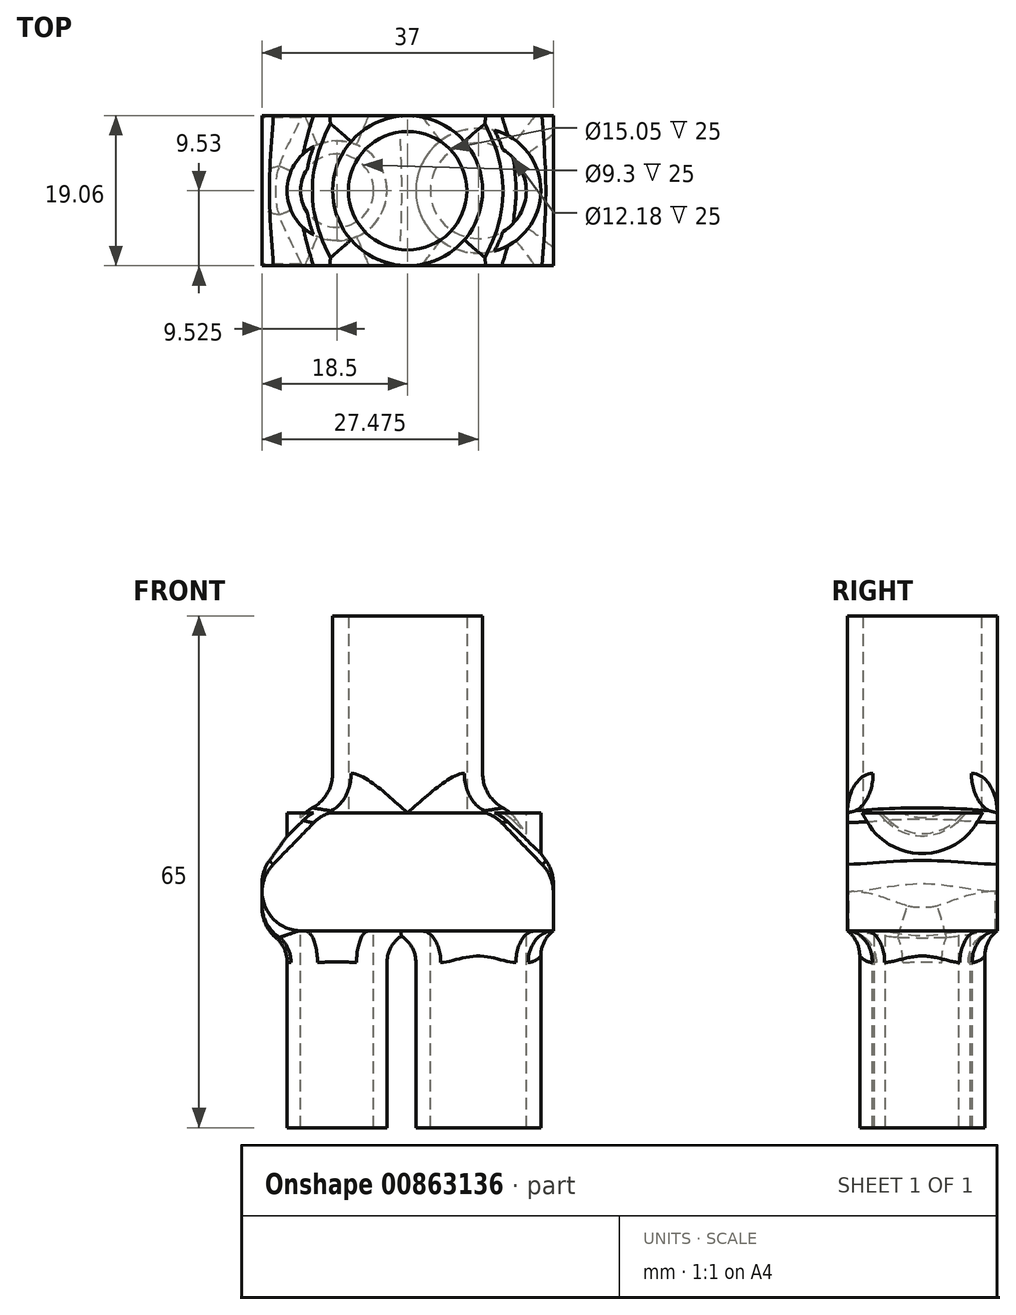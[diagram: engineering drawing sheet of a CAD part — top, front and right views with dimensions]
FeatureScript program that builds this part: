
annotation { "Feature Type Name" : "Feature", "Feature Type Description" : "" }
export const myFeature = defineFeature(function(context is Context, id is Id, definition is map)
    precondition{}
    {
        {
            var Q0;
            Q0=qCreatedBy(makeId("Top.planeOp"),FACE);
            var sketch = newSketch(context, id + "F0", { "sketchPlane" : qUnion([Q0])});
            skCircle(sketch, "E0", {"center": v(0, 0) * mm, "radius": 9.53 * mm});
            skCircle(sketch, "E1", {"center": v(0, 0) * mm, "radius": 7.53 * mm});
            skLineSegment(sketch, "E2.bottom", {"start": v(18.5, 9.53) * mm, "end": v(-18.5, 9.53) * mm});
            skLineSegment(sketch, "E2.top", {"start": v(18.5, -9.53) * mm, "end": v(-18.5, -9.53) * mm});
            skLineSegment(sketch, "E2.left", {"start": v(18.5, 9.53) * mm, "end": v(18.5, -9.53) * mm});
            skLineSegment(sketch, "E2.right", {"start": v(-18.5, 9.53) * mm, "end": v(-18.5, -9.53) * mm});
            skPoint(sketch, "E3", {"position": v(-8.98, 0) * mm});
            skPoint(sketch, "E4", {"position": v(8.97, 0) * mm});
            skCircle(sketch, "E5", {"center": v(-8.98, 0) * mm, "radius": 6.35 * mm});
            skCircle(sketch, "E6", {"center": v(8.97, 0) * mm, "radius": 7.94 * mm});
            skCircle(sketch, "E7", {"center": v(-8.98, 0) * mm, "radius": 4.65 * mm});
            skCircle(sketch, "E8", {"center": v(8.97, 0) * mm, "radius": 6.09 * mm});
            skSolve(sketch);
        }
        {
            var Q0;
            Q0=makeQuery(id+"F0.imprint","IMPRINT",FACE,{"disambiguationData":[TD([[makeQuery(id+"F0.imprint","IMPRINT",EDGE,{"derivedFrom":sQuery(id+"F0.wireOp",EDGE,"E0")}),1.0]])]});
            var Q1;
            {var subQ0=sQuery(id+"F0.wireOp",EDGE,"E7");var subQ1=sQuery(id+"F0.wireOp",EDGE,"E0");var subQ2=makeQuery(id+"F0.imprint","INTERSECT",VERTEX,{"disambiguationData":[OD(0.0)],"derivedFrom":[subQ1,subQ0]});Q1=makeQuery(id+"F0.imprint","IMPRINT",FACE,{"disambiguationData":[TD([[makeQuery(id+"F0.imprint","IMPRINT",EDGE,{"disambiguationData":[TD([[subQ2,-1.0]])],"derivedFrom":subQ1}),1.0]])]});}
            var Q2;
            {var subQ0=sQuery(id+"F0.wireOp",EDGE,"E7");var subQ1=sQuery(id+"F0.wireOp",EDGE,"E0");var subQ2=makeQuery(id+"F0.imprint","INTERSECT",VERTEX,{"disambiguationData":[OD(1.0)],"derivedFrom":[subQ1,subQ0]});Q2=makeQuery(id+"F0.imprint","IMPRINT",FACE,{"disambiguationData":[TD([[makeQuery(id+"F0.imprint","IMPRINT",EDGE,{"disambiguationData":[TD([[subQ2,-1.0]])],"derivedFrom":subQ1}),1.0]])]});}
            var Q3;
            {var subQ0=sQuery(id+"F0.wireOp",EDGE,"E6");var subQ1=sQuery(id+"F0.wireOp",EDGE,"E0");var subQ2=makeQuery(id+"F0.imprint","INTERSECT",VERTEX,{"disambiguationData":[OD(1.0)],"derivedFrom":[subQ1,subQ0]});Q3=makeQuery(id+"F0.imprint","IMPRINT",FACE,{"disambiguationData":[TD([[makeQuery(id+"F0.imprint","IMPRINT",EDGE,{"disambiguationData":[TD([[subQ2,-1.0]])],"derivedFrom":subQ1}),1.0]])]});}
            var Q4;
            {var subQ0=sQuery(id+"F0.wireOp",EDGE,"E8");var subQ1=sQuery(id+"F0.wireOp",EDGE,"E0");var subQ2=makeQuery(id+"F0.imprint","INTERSECT",VERTEX,{"disambiguationData":[OD(0.0)],"derivedFrom":[subQ1,subQ0]});Q4=makeQuery(id+"F0.imprint","IMPRINT",FACE,{"disambiguationData":[TD([[makeQuery(id+"F0.imprint","IMPRINT",EDGE,{"disambiguationData":[TD([[subQ2,1.0]])],"derivedFrom":subQ1}),1.0]])]});}
            var Q5;
            {var subQ0=sQuery(id+"F0.wireOp",EDGE,"E6");var subQ1=sQuery(id+"F0.wireOp",EDGE,"E0");var subQ2=makeQuery(id+"F0.imprint","INTERSECT",VERTEX,{"disambiguationData":[OD(0.0)],"derivedFrom":[subQ1,subQ0]});Q5=makeQuery(id+"F0.imprint","IMPRINT",FACE,{"disambiguationData":[TD([[makeQuery(id+"F0.imprint","IMPRINT",EDGE,{"disambiguationData":[TD([[subQ2,1.0]])],"derivedFrom":subQ1}),1.0]])]});}
            var Q6;
            {var subQ0=sQuery(id+"F0.wireOp",EDGE,"E5");var subQ1=sQuery(id+"F0.wireOp",EDGE,"E0");var subQ2=makeQuery(id+"F0.imprint","INTERSECT",VERTEX,{"disambiguationData":[OD(0.0)],"derivedFrom":[subQ1,subQ0]});Q6=makeQuery(id+"F0.imprint","IMPRINT",FACE,{"disambiguationData":[TD([[makeQuery(id+"F0.imprint","IMPRINT",EDGE,{"disambiguationData":[TD([[subQ2,-1.0]])],"derivedFrom":subQ1}),1.0]])]});}
            extrude(context, id + "F1", {"entities" : qUnion([Q0, Q1, Q2, Q3, Q4, Q5, Q6]), "depth" : 25 * mm, "offsetDistance" : 25 * mm});
        }
        {
            var Q0;
            {var subQ0=sQuery(id+"F0.wireOp",EDGE,"E6");var subQ1=sQuery(id+"F0.wireOp",EDGE,"E1");var subQ2=makeQuery(id+"F0.imprint","INTERSECT",VERTEX,{"disambiguationData":[OD(0.0)],"derivedFrom":[subQ1,subQ0]});Q0=makeQuery(id+"F0.imprint","IMPRINT",FACE,{"disambiguationData":[TD([[makeQuery(id+"F0.imprint","IMPRINT",EDGE,{"disambiguationData":[TD([[subQ2,1.0]])],"derivedFrom":subQ1}),1.0]])]});}
            var Q1;
            {var subQ0=sQuery(id+"F0.wireOp",EDGE,"E5");var subQ1=sQuery(id+"F0.wireOp",EDGE,"E1");var subQ2=makeQuery(id+"F0.imprint","INTERSECT",VERTEX,{"disambiguationData":[OD(0.0)],"derivedFrom":[subQ1,subQ0]});Q1=makeQuery(id+"F0.imprint","IMPRINT",FACE,{"disambiguationData":[TD([[makeQuery(id+"F0.imprint","IMPRINT",EDGE,{"disambiguationData":[TD([[subQ2,-1.0]])],"derivedFrom":subQ1}),1.0]])]});}
            var Q2;
            {var subQ0=sQuery(id+"F0.wireOp",EDGE,"E2.right");Q2=makeQuery(id+"F0.imprint","IMPRINT",FACE,{"disambiguationData":[TD([[makeQuery(id+"F0.imprint","IMPRINT",EDGE,{"derivedFrom":subQ0}),1.0]])]});}
            var Q3;
            {var subQ0=sQuery(id+"F0.wireOp",EDGE,"E2.left");Q3=makeQuery(id+"F0.imprint","IMPRINT",FACE,{"disambiguationData":[TD([[makeQuery(id+"F0.imprint","IMPRINT",EDGE,{"derivedFrom":subQ0}),-1.0]])]});}
            var Q4;
            {var subQ0=sQuery(id+"F0.wireOp",EDGE,"E6");var subQ1=sQuery(id+"F0.wireOp",EDGE,"E0");var subQ2=makeQuery(id+"F0.imprint","INTERSECT",VERTEX,{"disambiguationData":[OD(0.0)],"derivedFrom":[subQ1,subQ0]});Q4=makeQuery(id+"F0.imprint","IMPRINT",FACE,{"disambiguationData":[TD([[makeQuery(id+"F0.imprint","IMPRINT",EDGE,{"disambiguationData":[TD([[subQ2,1.0]])],"derivedFrom":subQ1}),1.0]])]});}
            var Q5;
            {var subQ0=sQuery(id+"F0.wireOp",EDGE,"E5");var subQ1=sQuery(id+"F0.wireOp",EDGE,"E0");var subQ2=makeQuery(id+"F0.imprint","INTERSECT",VERTEX,{"disambiguationData":[OD(0.0)],"derivedFrom":[subQ1,subQ0]});Q5=makeQuery(id+"F0.imprint","IMPRINT",FACE,{"disambiguationData":[TD([[makeQuery(id+"F0.imprint","IMPRINT",EDGE,{"disambiguationData":[TD([[subQ2,-1.0]])],"derivedFrom":subQ1}),1.0]])]});}
            var Q6;
            {var subQ0=sQuery(id+"F0.wireOp",EDGE,"E7");var subQ1=sQuery(id+"F0.wireOp",EDGE,"E0");var subQ2=makeQuery(id+"F0.imprint","INTERSECT",VERTEX,{"disambiguationData":[OD(0.0)],"derivedFrom":[subQ1,subQ0]});Q6=makeQuery(id+"F0.imprint","IMPRINT",FACE,{"disambiguationData":[TD([[makeQuery(id+"F0.imprint","IMPRINT",EDGE,{"disambiguationData":[TD([[subQ2,-1.0]])],"derivedFrom":subQ1}),1.0]])]});}
            var Q7;
            {var subQ0=sQuery(id+"F0.wireOp",EDGE,"E7");var subQ1=sQuery(id+"F0.wireOp",EDGE,"E0");var subQ2=makeQuery(id+"F0.imprint","INTERSECT",VERTEX,{"disambiguationData":[OD(1.0)],"derivedFrom":[subQ1,subQ0]});Q7=makeQuery(id+"F0.imprint","IMPRINT",FACE,{"disambiguationData":[TD([[makeQuery(id+"F0.imprint","IMPRINT",EDGE,{"disambiguationData":[TD([[subQ2,-1.0]])],"derivedFrom":subQ1}),1.0]])]});}
            var Q8;
            {var subQ0=sQuery(id+"F0.wireOp",EDGE,"E6");var subQ1=sQuery(id+"F0.wireOp",EDGE,"E0");var subQ2=makeQuery(id+"F0.imprint","INTERSECT",VERTEX,{"disambiguationData":[OD(1.0)],"derivedFrom":[subQ1,subQ0]});Q8=makeQuery(id+"F0.imprint","IMPRINT",FACE,{"disambiguationData":[TD([[makeQuery(id+"F0.imprint","IMPRINT",EDGE,{"disambiguationData":[TD([[subQ2,-1.0]])],"derivedFrom":subQ1}),1.0]])]});}
            var Q9;
            {var subQ0=sQuery(id+"F0.wireOp",EDGE,"E8");var subQ1=sQuery(id+"F0.wireOp",EDGE,"E0");var subQ2=makeQuery(id+"F0.imprint","INTERSECT",VERTEX,{"disambiguationData":[OD(0.0)],"derivedFrom":[subQ1,subQ0]});Q9=makeQuery(id+"F0.imprint","IMPRINT",FACE,{"disambiguationData":[TD([[makeQuery(id+"F0.imprint","IMPRINT",EDGE,{"disambiguationData":[TD([[subQ2,1.0]])],"derivedFrom":subQ1}),1.0]])]});}
            var Q10;
            {var subQ0=sQuery(id+"F0.wireOp",EDGE,"E7");var subQ1=sQuery(id+"F0.wireOp",EDGE,"E0");var subQ2=makeQuery(id+"F0.imprint","INTERSECT",VERTEX,{"disambiguationData":[OD(0.0)],"derivedFrom":[subQ1,subQ0]});Q10=makeQuery(id+"F0.imprint","IMPRINT",FACE,{"disambiguationData":[TD([[makeQuery(id+"F0.imprint","IMPRINT",EDGE,{"disambiguationData":[TD([[subQ2,-1.0]])],"derivedFrom":subQ1}),-1.0]])]});}
            var Q11;
            {var subQ0=sQuery(id+"F0.wireOp",EDGE,"E5");var subQ1=sQuery(id+"F0.wireOp",EDGE,"E0");var subQ2=makeQuery(id+"F0.imprint","INTERSECT",VERTEX,{"disambiguationData":[OD(0.0)],"derivedFrom":[subQ1,subQ0]});Q11=makeQuery(id+"F0.imprint","IMPRINT",FACE,{"disambiguationData":[TD([[makeQuery(id+"F0.imprint","IMPRINT",EDGE,{"disambiguationData":[TD([[subQ2,-1.0]])],"derivedFrom":subQ1}),-1.0]])]});}
            var Q12;
            {var subQ0=sQuery(id+"F0.wireOp",EDGE,"E8");var subQ1=sQuery(id+"F0.wireOp",EDGE,"E1");var subQ2=makeQuery(id+"F0.imprint","INTERSECT",VERTEX,{"disambiguationData":[OD(0.0)],"derivedFrom":[subQ1,subQ0]});Q12=makeQuery(id+"F0.imprint","IMPRINT",FACE,{"disambiguationData":[TD([[makeQuery(id+"F0.imprint","IMPRINT",EDGE,{"disambiguationData":[TD([[subQ2,1.0]])],"derivedFrom":subQ1}),1.0]])]});}
            var Q13;
            {var subQ0=sQuery(id+"F0.wireOp",EDGE,"E8");var subQ1=sQuery(id+"F0.wireOp",EDGE,"E0");var subQ2=makeQuery(id+"F0.imprint","INTERSECT",VERTEX,{"disambiguationData":[OD(0.0)],"derivedFrom":[subQ1,subQ0]});Q13=makeQuery(id+"F0.imprint","IMPRINT",FACE,{"disambiguationData":[TD([[makeQuery(id+"F0.imprint","IMPRINT",EDGE,{"disambiguationData":[TD([[subQ2,1.0]])],"derivedFrom":subQ1}),-1.0]])]});}
            var Q14;
            {var subQ0=sQuery(id+"F0.wireOp",EDGE,"E6");var subQ1=sQuery(id+"F0.wireOp",EDGE,"E0");var subQ2=makeQuery(id+"F0.imprint","INTERSECT",VERTEX,{"disambiguationData":[OD(0.0)],"derivedFrom":[subQ1,subQ0]});Q14=makeQuery(id+"F0.imprint","IMPRINT",FACE,{"disambiguationData":[TD([[makeQuery(id+"F0.imprint","IMPRINT",EDGE,{"disambiguationData":[TD([[subQ2,1.0]])],"derivedFrom":subQ1}),-1.0]])]});}
            var Q15;
            {var subQ0=sQuery(id+"F0.wireOp",EDGE,"E6");var subQ1=sQuery(id+"F0.wireOp",EDGE,"E1");var subQ2=makeQuery(id+"F0.imprint","INTERSECT",VERTEX,{"disambiguationData":[OD(0.0)],"derivedFrom":[subQ1,subQ0]});Q15=makeQuery(id+"F0.imprint","IMPRINT",FACE,{"disambiguationData":[TD([[makeQuery(id+"F0.imprint","IMPRINT",EDGE,{"disambiguationData":[TD([[subQ2,-1.0]])],"derivedFrom":subQ1}),1.0]])]});}
            var Q16;
            {var subQ5=sQuery(id+"F0.wireOp",EDGE,"E0");var subQ7=makeQuery(id+"F0.imprint","INTERSECT",VERTEX,{"derivedFrom":[subQ5,sQuery(id+"F0.wireOp",EDGE,"E2.top")]});Q16=makeQuery(id+"F0.imprint","IMPRINT",FACE,{"disambiguationData":[TD([[makeQuery(id+"F0.imprint","IMPRINT",EDGE,{"disambiguationData":[TD([[subQ7,1.0]])],"derivedFrom":subQ5}),1.0]])]});}
            var Q17;
            {var subQ1=sQuery(id+"F0.wireOp",EDGE,"E0");var subQ5=makeQuery(id+"F0.imprint","INTERSECT",VERTEX,{"derivedFrom":[subQ1,sQuery(id+"F0.wireOp",EDGE,"E2.bottom")]});Q17=makeQuery(id+"F0.imprint","IMPRINT",FACE,{"disambiguationData":[TD([[makeQuery(id+"F0.imprint","IMPRINT",EDGE,{"disambiguationData":[TD([[subQ5,1.0]])],"derivedFrom":subQ1}),1.0]])]});}
            var Q18;
            {var subQ0=sQuery(id+"F0.wireOp",EDGE,"E7");var subQ1=sQuery(id+"F0.wireOp",EDGE,"E1");var subQ2=makeQuery(id+"F0.imprint","INTERSECT",VERTEX,{"disambiguationData":[OD(0.0)],"derivedFrom":[subQ1,subQ0]});Q18=makeQuery(id+"F0.imprint","IMPRINT",FACE,{"disambiguationData":[TD([[makeQuery(id+"F0.imprint","IMPRINT",EDGE,{"disambiguationData":[TD([[subQ2,-1.0]])],"derivedFrom":subQ1}),1.0]])]});}
            extrude(context, id + "F2", {"entities" : qUnion([Q0, Q1, Q2, Q3, Q4, Q5, Q6, Q7, Q8, Q9, Q10, Q11, Q12, Q13, Q14, Q15, Q16, Q17, Q18]), "operationType" : NewBodyOperationType.ADD, "oppositeDirection" : true, "depth" : 15 * mm, "offsetDistance" : 25 * mm});
        }
        {
            var Q0;
            Q0=makeQuery(id+"F2.boolean.opBoolean","SPLIT",EDGE,{"disambiguationData":[OD(0.0)],"derivedFrom":makeQuery(id+"F1.opExtrude","CAP_EDGE",EDGE,{"disambiguationData":[OSD([sQuery(id+"F0.wireOp",EDGE,"E0")])],"isStart":true})});
            var Q1;
            Q1=makeQuery(id+"F2.boolean.opBoolean","SPLIT",EDGE,{"disambiguationData":[OD(1.0)],"derivedFrom":makeQuery(id+"F1.opExtrude","CAP_EDGE",EDGE,{"disambiguationData":[OSD([sQuery(id+"F0.wireOp",EDGE,"E0")])],"isStart":true})});
            fillet(context, id + "F3", {"entities" : qUnion([Q0, Q1]), "radius" : 5 * mm, "tangentPropagation" : true, "allowEdgeOverflow" : false});
        }
        {
            var Q0;
            Q0=makeQuery(id+"F2.opExtrude","CAP_EDGE",EDGE,{"disambiguationData":[OSD([sQuery(id+"F0.wireOp",EDGE,"E2.left")])],"isStart":true});
            var Q1;
            Q1=makeQuery(id+"F2.opExtrude","CAP_EDGE",EDGE,{"disambiguationData":[OSD([sQuery(id+"F0.wireOp",EDGE,"E2.right")])],"isStart":true});
            chamfer(context, id + "F4", {"entities" : qUnion([Q0, Q1]), "width" : 8 * mm, "tangentPropagation" : true});
        }
        {
            var Q0;
            {var subQ0=sQuery(id+"F0.wireOp",EDGE,"E0");Q0=makeQuery(id+"F4.opChamfer","BLEND_EDGE",EDGE,{"blendedFrom":[makeQuery(id+"F2.opExtrude","CAP_EDGE",EDGE,{"disambiguationData":[OSD([sQuery(id+"F0.wireOp",EDGE,"E2.right")])],"isStart":true}),makeQuery(id+"F3.opFillet","BLEND_FACE",FACE,{"disambiguationData":[OSD([subQ0]),TDD([makeQuery(id+"F2.boolean.opBoolean","SPLIT",EDGE,{"disambiguationData":[OD(1.0)],"derivedFrom":makeQuery(id+"F1.opExtrude","CAP_EDGE",EDGE,{"disambiguationData":[OSD([subQ0])],"isStart":true})})]),OD(2.0)]})],"blendedInto":[makeQuery(id+"F3.opFillet","BLEND_FACE",FACE,{"disambiguationData":[OSD([subQ0]),TDD([makeQuery(id+"F2.boolean.opBoolean","SPLIT",EDGE,{"disambiguationData":[OD(1.0)],"derivedFrom":makeQuery(id+"F1.opExtrude","CAP_EDGE",EDGE,{"disambiguationData":[OSD([subQ0])],"isStart":true})})]),OD(2.0)]})]});}
            var Q1;
            {var subQ0=sQuery(id+"F0.wireOp",EDGE,"E0");Q1=makeQuery(id+"F4.opChamfer","BLEND_EDGE",EDGE,{"blendedFrom":[makeQuery(id+"F2.opExtrude","CAP_EDGE",EDGE,{"disambiguationData":[OSD([sQuery(id+"F0.wireOp",EDGE,"E2.left")])],"isStart":true}),makeQuery(id+"F3.opFillet","BLEND_FACE",FACE,{"disambiguationData":[OSD([subQ0]),TDD([makeQuery(id+"F2.boolean.opBoolean","SPLIT",EDGE,{"disambiguationData":[OD(0.0)],"derivedFrom":makeQuery(id+"F1.opExtrude","CAP_EDGE",EDGE,{"disambiguationData":[OSD([subQ0])],"isStart":true})})]),OD(2.0)]})],"blendedInto":[makeQuery(id+"F3.opFillet","BLEND_FACE",FACE,{"disambiguationData":[OSD([subQ0]),TDD([makeQuery(id+"F2.boolean.opBoolean","SPLIT",EDGE,{"disambiguationData":[OD(0.0)],"derivedFrom":makeQuery(id+"F1.opExtrude","CAP_EDGE",EDGE,{"disambiguationData":[OSD([subQ0])],"isStart":true})})]),OD(2.0)]})]});}
            var Q2;
            {var subQ0=sQuery(id+"F0.wireOp",EDGE,"E2.left");Q2=makeQuery(id+"F4.opChamfer","BLEND_EDGE",EDGE,{"blendedFrom":[makeQuery(id+"F2.opExtrude","CAP_EDGE",EDGE,{"disambiguationData":[OSD([subQ0])],"isStart":true}),makeQuery(id+"F2.opExtrude","SWEPT_FACE",FACE,{"disambiguationData":[OSD([subQ0])]})],"blendedInto":[makeQuery(id+"F2.opExtrude","SWEPT_FACE",FACE,{"disambiguationData":[OSD([subQ0])]})]});}
            var Q3;
            {var subQ0=sQuery(id+"F0.wireOp",EDGE,"E2.right");Q3=makeQuery(id+"F4.opChamfer","BLEND_EDGE",EDGE,{"blendedFrom":[makeQuery(id+"F2.opExtrude","CAP_EDGE",EDGE,{"disambiguationData":[OSD([subQ0])],"isStart":true}),makeQuery(id+"F2.opExtrude","SWEPT_FACE",FACE,{"disambiguationData":[OSD([subQ0])]})],"blendedInto":[makeQuery(id+"F2.opExtrude","SWEPT_FACE",FACE,{"disambiguationData":[OSD([subQ0])]})]});}
            fillet(context, id + "F5", {"entities" : qUnion([Q0, Q1, Q2, Q3]), "radius" : 5 * mm, "tangentPropagation" : true, "allowEdgeOverflow" : false});
        }
        {
            var Q0;
            {var subQ0=sQuery(id+"F0.wireOp",EDGE,"E5");var subQ1=sQuery(id+"F0.wireOp",EDGE,"E0");var subQ2=makeQuery(id+"F0.imprint","INTERSECT",VERTEX,{"disambiguationData":[OD(0.0)],"derivedFrom":[subQ1,subQ0]});Q0=makeQuery(id+"F0.imprint","IMPRINT",FACE,{"disambiguationData":[TD([[makeQuery(id+"F0.imprint","IMPRINT",EDGE,{"disambiguationData":[TD([[subQ2,-1.0]])],"derivedFrom":subQ1}),-1.0]])]});}
            var Q1;
            {var subQ0=sQuery(id+"F0.wireOp",EDGE,"E7");var subQ1=sQuery(id+"F0.wireOp",EDGE,"E0");var subQ2=makeQuery(id+"F0.imprint","INTERSECT",VERTEX,{"disambiguationData":[OD(1.0)],"derivedFrom":[subQ1,subQ0]});Q1=makeQuery(id+"F0.imprint","IMPRINT",FACE,{"disambiguationData":[TD([[makeQuery(id+"F0.imprint","IMPRINT",EDGE,{"disambiguationData":[TD([[subQ2,-1.0]])],"derivedFrom":subQ1}),1.0]])]});}
            var Q2;
            {var subQ0=sQuery(id+"F0.wireOp",EDGE,"E5");var subQ1=sQuery(id+"F0.wireOp",EDGE,"E1");var subQ2=makeQuery(id+"F0.imprint","INTERSECT",VERTEX,{"disambiguationData":[OD(0.0)],"derivedFrom":[subQ1,subQ0]});Q2=makeQuery(id+"F0.imprint","IMPRINT",FACE,{"disambiguationData":[TD([[makeQuery(id+"F0.imprint","IMPRINT",EDGE,{"disambiguationData":[TD([[subQ2,-1.0]])],"derivedFrom":subQ1}),1.0]])]});}
            var Q3;
            {var subQ0=sQuery(id+"F0.wireOp",EDGE,"E5");var subQ1=sQuery(id+"F0.wireOp",EDGE,"E0");var subQ2=makeQuery(id+"F0.imprint","INTERSECT",VERTEX,{"disambiguationData":[OD(0.0)],"derivedFrom":[subQ1,subQ0]});Q3=makeQuery(id+"F0.imprint","IMPRINT",FACE,{"disambiguationData":[TD([[makeQuery(id+"F0.imprint","IMPRINT",EDGE,{"disambiguationData":[TD([[subQ2,-1.0]])],"derivedFrom":subQ1}),1.0]])]});}
            var Q4;
            {var subQ0=sQuery(id+"F0.wireOp",EDGE,"E6");var subQ1=sQuery(id+"F0.wireOp",EDGE,"E1");var subQ2=makeQuery(id+"F0.imprint","INTERSECT",VERTEX,{"disambiguationData":[OD(0.0)],"derivedFrom":[subQ1,subQ0]});Q4=makeQuery(id+"F0.imprint","IMPRINT",FACE,{"disambiguationData":[TD([[makeQuery(id+"F0.imprint","IMPRINT",EDGE,{"disambiguationData":[TD([[subQ2,1.0]])],"derivedFrom":subQ1}),1.0]])]});}
            var Q5;
            {var subQ0=sQuery(id+"F0.wireOp",EDGE,"E6");var subQ1=sQuery(id+"F0.wireOp",EDGE,"E0");var subQ2=makeQuery(id+"F0.imprint","INTERSECT",VERTEX,{"disambiguationData":[OD(0.0)],"derivedFrom":[subQ1,subQ0]});Q5=makeQuery(id+"F0.imprint","IMPRINT",FACE,{"disambiguationData":[TD([[makeQuery(id+"F0.imprint","IMPRINT",EDGE,{"disambiguationData":[TD([[subQ2,1.0]])],"derivedFrom":subQ1}),1.0]])]});}
            var Q6;
            {var subQ0=sQuery(id+"F0.wireOp",EDGE,"E6");var subQ1=sQuery(id+"F0.wireOp",EDGE,"E0");var subQ2=makeQuery(id+"F0.imprint","INTERSECT",VERTEX,{"disambiguationData":[OD(1.0)],"derivedFrom":[subQ1,subQ0]});Q6=makeQuery(id+"F0.imprint","IMPRINT",FACE,{"disambiguationData":[TD([[makeQuery(id+"F0.imprint","IMPRINT",EDGE,{"disambiguationData":[TD([[subQ2,-1.0]])],"derivedFrom":subQ1}),1.0]])]});}
            var Q7;
            {var subQ0=sQuery(id+"F0.wireOp",EDGE,"E6");var subQ1=sQuery(id+"F0.wireOp",EDGE,"E0");var subQ2=makeQuery(id+"F0.imprint","INTERSECT",VERTEX,{"disambiguationData":[OD(0.0)],"derivedFrom":[subQ1,subQ0]});Q7=makeQuery(id+"F0.imprint","IMPRINT",FACE,{"disambiguationData":[TD([[makeQuery(id+"F0.imprint","IMPRINT",EDGE,{"disambiguationData":[TD([[subQ2,1.0]])],"derivedFrom":subQ1}),-1.0]])]});}
            extrude(context, id + "F6", {"entities" : qUnion([Q0, Q1, Q2, Q3, Q4, Q5, Q6, Q7]), "operationType" : NewBodyOperationType.ADD, "oppositeDirection" : true, "depth" : 40 * mm, "offsetDistance" : 25 * mm});
        }
        {
            var Q0;
            Q0=makeQuery(id+"F6.boolean.opBoolean","INTERSECT",EDGE,{"derivedFrom":[makeQuery(id+"F2.opExtrude","CAP_FACE",FACE,{"disambiguationData":[OSD([sQuery(id+"F0.wireOp",EDGE,"E2.bottom"),sQuery(id+"F0.wireOp",EDGE,"E2.top"),sQuery(id+"F0.wireOp",EDGE,"E2.left"),sQuery(id+"F0.wireOp",EDGE,"E2.right")])],"isStart":false}),makeQuery(id+"F6.opExtrude","SWEPT_FACE",FACE,{"disambiguationData":[OSD([sQuery(id+"F0.wireOp",EDGE,"E5")])]})]});
            var Q1;
            Q1=makeQuery(id+"F6.boolean.opBoolean","INTERSECT",EDGE,{"derivedFrom":[makeQuery(id+"F2.opExtrude","CAP_FACE",FACE,{"disambiguationData":[OSD([sQuery(id+"F0.wireOp",EDGE,"E2.bottom"),sQuery(id+"F0.wireOp",EDGE,"E2.top"),sQuery(id+"F0.wireOp",EDGE,"E2.left"),sQuery(id+"F0.wireOp",EDGE,"E2.right")])],"isStart":false}),makeQuery(id+"F6.opExtrude","SWEPT_FACE",FACE,{"disambiguationData":[OSD([sQuery(id+"F0.wireOp",EDGE,"E6")])]})]});
            fillet(context, id + "F7", {"entities" : qUnion([Q0, Q1]), "radius" : 4 * mm, "tangentPropagation" : true, "allowEdgeOverflow" : false});
        }
        {
            var Q0;
            {var subQ0=sQuery(id+"F0.wireOp",EDGE,"E2.right");Q0=makeQuery(id+"F7.opFillet","BLEND_EDGE",EDGE,{"blendedFrom":[makeQuery(id+"F6.boolean.opBoolean","INTERSECT",EDGE,{"derivedFrom":[makeQuery(id+"F2.opExtrude","CAP_FACE",FACE,{"disambiguationData":[OSD([sQuery(id+"F0.wireOp",EDGE,"E2.bottom"),sQuery(id+"F0.wireOp",EDGE,"E2.top"),sQuery(id+"F0.wireOp",EDGE,"E2.left"),subQ0])],"isStart":false}),makeQuery(id+"F6.opExtrude","SWEPT_FACE",FACE,{"disambiguationData":[OSD([sQuery(id+"F0.wireOp",EDGE,"E5")])]})]}),makeQuery(id+"F2.opExtrude","SWEPT_FACE",FACE,{"disambiguationData":[OSD([subQ0])]})],"blendedInto":[makeQuery(id+"F2.opExtrude","SWEPT_FACE",FACE,{"disambiguationData":[OSD([subQ0])]})]});}
            fillet(context, id + "F8", {"entities" : qUnion([Q0]), "radius" : 5 * mm, "tangentPropagation" : true, "allowEdgeOverflow" : false});
        }
    });
